# Revit family: 304_Cim717PLF-_
name_source: partatom
category: Pipe Accessories
revit_build: Autodesk Revit 2017 (Build: 20160225_1515(x64)
units: mm (PartAtom-declared; Revit-internal decimal feet)

## family parameters
Always vertical = Yes
Cut with Voids When Loaded = No
Part Type = Valve - Breaks Into
Round Connector Dimension = Use Diameter
Shared = No
Work Plane-Based = No

## types (2) — shared parameters
A = 35 mm  [stored 0.114829 ft]
A1 = 32 mm  [stored 0.104987 ft]
CAT0 = Yes
CH = 20 mm  [stored 0.0656168 ft]
D2 = 16 mm  [stored 0.0524934 ft]
Description = AUTOMATIC BALANCING VALVE P.I.C.V. - PN 25 - "CR" BRASS - LOW FLOW
H1 = 25 mm  [stored 0.082021 ft]
H2 = 14 mm  [stored 0.0459318 ft]
H3 = 36 mm  [stored 0.11811 ft]
H4 = 55 mm  [stored 0.180446 ft]
H4__ve = -55 mm  [stored -0.180446 ft]
L2D_Min = 3048 mm  [stored 10 ft]
Manufacturer = Cimberio
QmdConnectorList = 301;D;302;D
URL = www.cimberio.it
magiPartTypeId = 304
magiProductFamilyId = Cim717PLF-*
zero-valued in all types: MC_Default_elevation

## per-type parameters (varying)
| type | D | D1 | L | L2 | L2D | LL | T | W2D |
| Cim717PLF-10 | 15 mm | 20 mm  [stored 0.0656168 ft] | 53 mm  [stored 0.173885 ft] | 10 mm  [stored 0.0328084 ft] | 53 mm  [stored 0.173885 ft] | 27 mm | 15 mm  [stored 0.0492126 ft] | 15 mm  [stored 0.0492126 ft] |
| Cim717PLF-15 | 20 mm | 26 mm  [stored 0.0853018 ft] | 65 mm  [stored 0.213255 ft] | 15 mm  [stored 0.0492126 ft] | 65 mm  [stored 0.213255 ft] | 33 mm | 20 mm  [stored 0.0656168 ft] | 20 mm  [stored 0.0656168 ft] |

note: column(s) folded — value = type name in every type: magiProductCode, magiProductId

note: [stored X ft] marks values corroborated as IEEE doubles in the binary element streams (Revit-internal decimal feet)

## geometry (parser evidence)
native form markers: Sweep x2
no freeform markers — native parametric forms only
